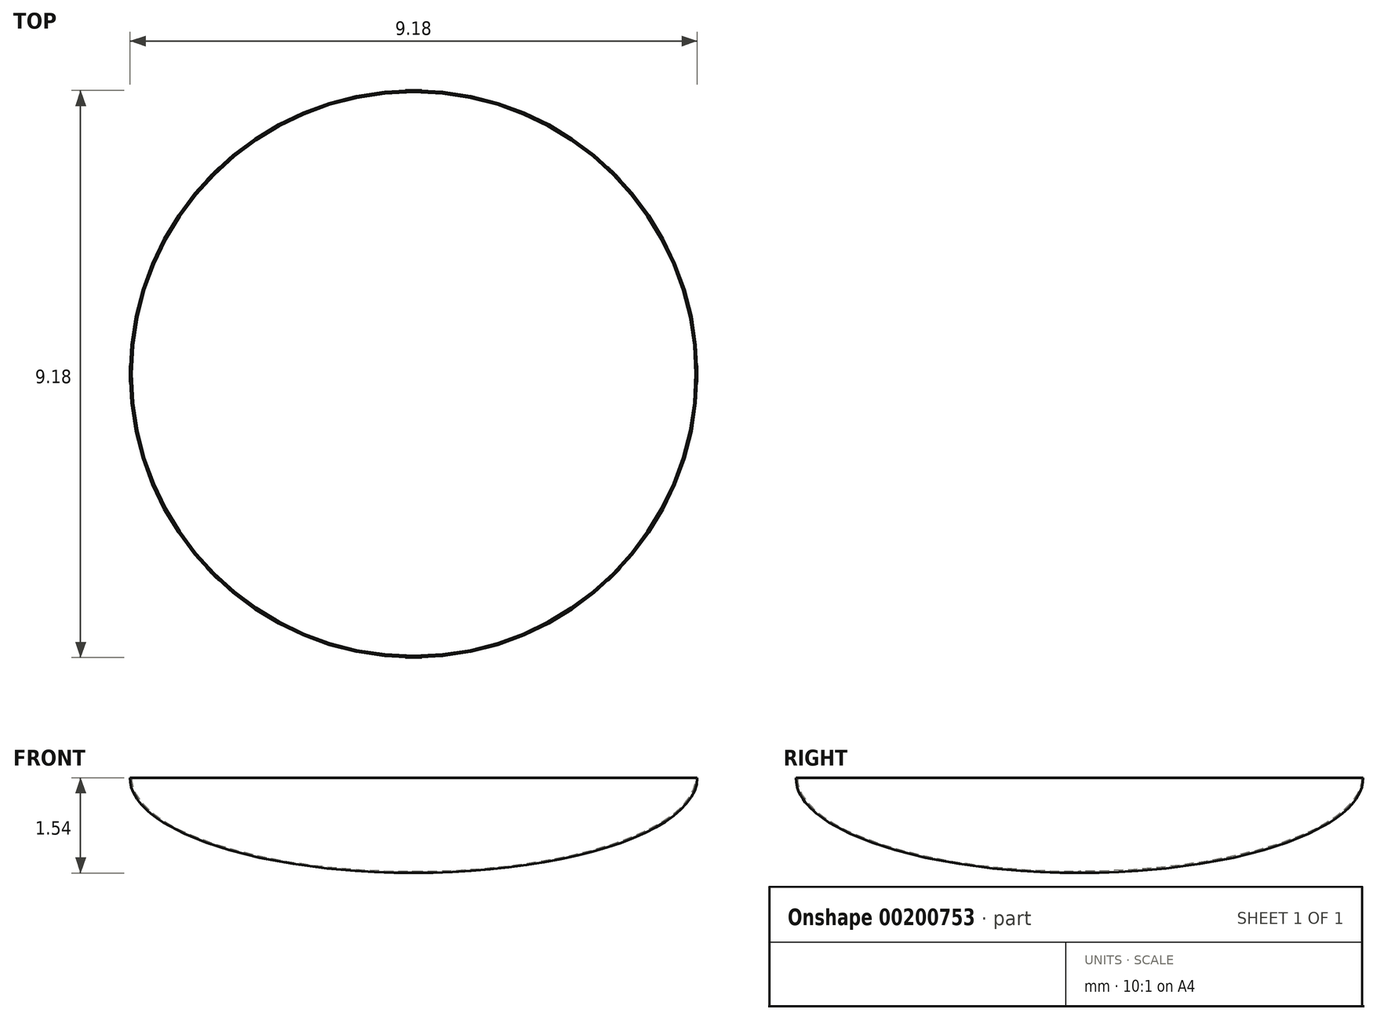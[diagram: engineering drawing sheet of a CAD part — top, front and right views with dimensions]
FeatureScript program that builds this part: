
annotation { "Feature Type Name" : "Feature", "Feature Type Description" : "" }
export const myFeature = defineFeature(function(context is Context, id is Id, definition is map)
    precondition{}
    {
        {
            var Q0;
            Q0=qCreatedBy(makeId("Front.planeOp"),FACE);
            var sketch = newSketch(context, id + "F0", { "sketchPlane" : qUnion([Q0])});
            skEllipticalArc(sketch, "E0", {});
            skLineSegment(sketch, "E1", {"start": v(0, 0) * mm, "end": v(4.6, 0) * mm});
            skLineSegment(sketch, "E2", {"start": v(0, 0) * mm, "end": v(0, -1.54) * mm});
            skPoint(sketch, "E3.orphan", {"position": v(-4.6, 0) * mm});
            const initialGuessF0  = {"E0": [0, 0, 1, 0, 0.004591240081936121, 0.001538975047878921, 4.71238898038469, 0]};
            skSetInitialGuess(sketch, initialGuessF0);
            skSolve(sketch);
        }
        {
            var Q0;
            Q0=makeQuery(id+"F0.imprint","IMPRINT",FACE,{"disambiguationData":[TD([[makeQuery(id+"F0.imprint","IMPRINT",EDGE,{"derivedFrom":sQuery(id+"F0.wireOp",EDGE,"E0")}),1.0]])]});
            var Q1;
            Q1=sQuery(id+"F0.wireOp",EDGE,"E2");
            revolve(context, id + "F1", {"entities" : qUnion([Q0]), "axis" : qUnion([Q1]), "revolveType" : RevolveType.FULL});
        }
        {
            var Q0;
            Q0=makeQuery(id+"F1.opRevolve","SWEPT_FACE",FACE,{"disambiguationData":[OSD([sQuery(id+"F0.wireOp",EDGE,"E1")])]});
            var Q1;
            Q1=makeQuery(id+"F1.opRevolve","SWEPT_BODY",BODY,{"disambiguationData":[OSD([sQuery(id+"F0.wireOp",EDGE,"E0"),sQuery(id+"F0.wireOp",EDGE,"E1"),sQuery(id+"F0.wireOp",EDGE,"E2")])]});
            shell(context, id + "F2", {"entities" : qUnion([Q0]), "parts" : qUnion([Q1]), "thickness" : 0.03 * mm});
        }
    });
